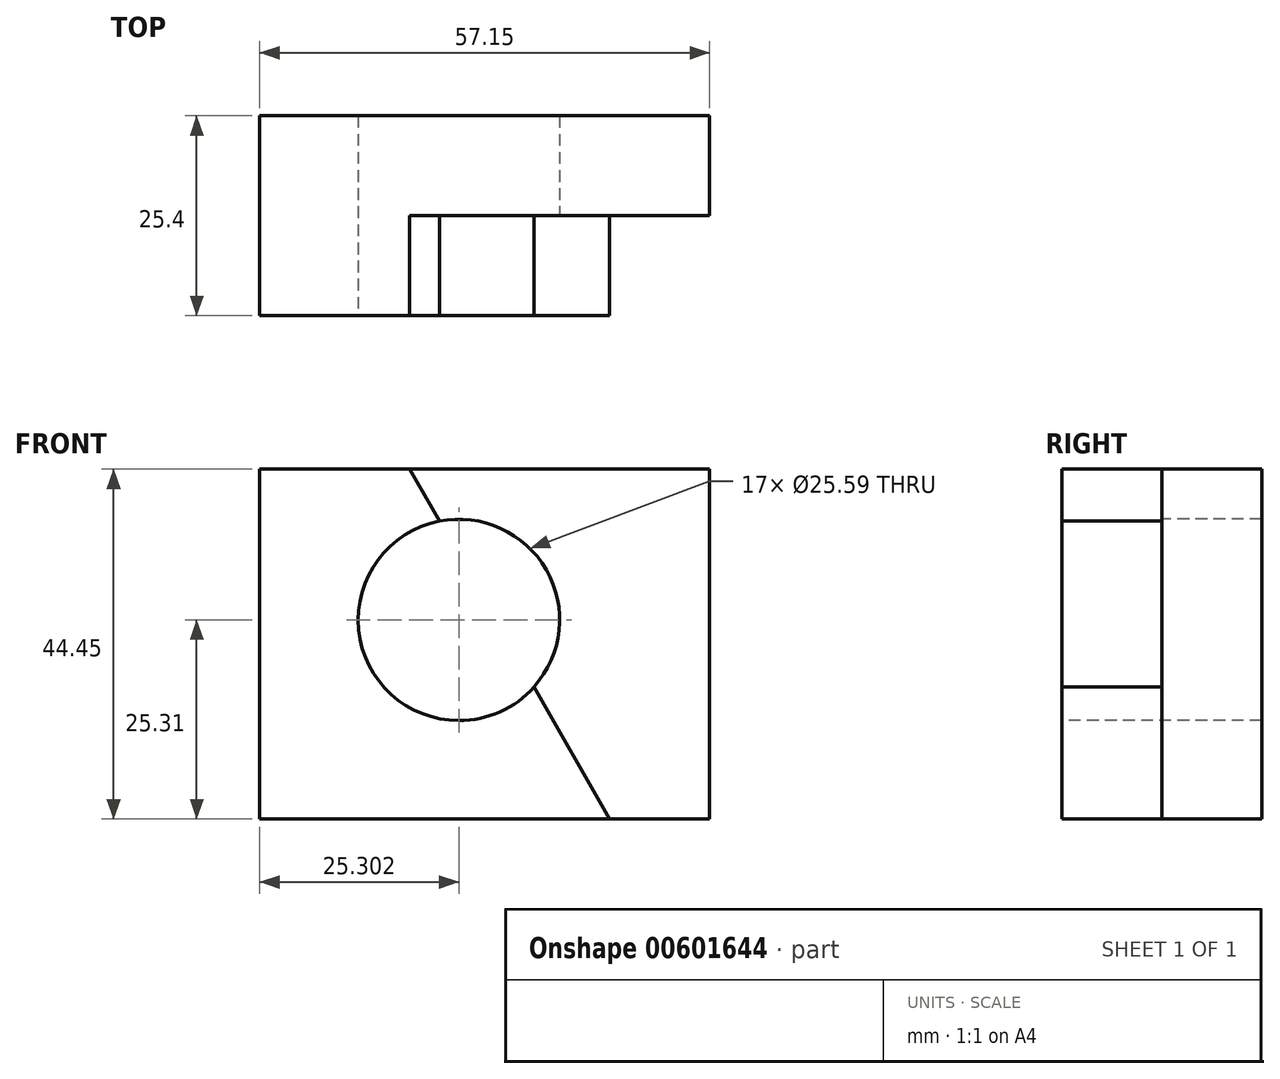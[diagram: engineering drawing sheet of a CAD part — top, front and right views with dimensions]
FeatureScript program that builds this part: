
annotation { "Feature Type Name" : "Feature", "Feature Type Description" : "" }
export const myFeature = defineFeature(function(context is Context, id is Id, definition is map)
    precondition{}
    {
        {
            var Q0;
            Q0=qCreatedBy(makeId("Front.planeOp"),FACE);
            var sketch = newSketch(context, id + "F0", { "sketchPlane" : qUnion([Q0])});
            skLineSegment(sketch, "E0", {"start": v(-65.96, 58.63) * mm, "end": v(-65.96, 14.18) * mm});
            skLineSegment(sketch, "E1", {"start": v(-65.96, 14.18) * mm, "end": v(-8.81, 14.18) * mm});
            skLineSegment(sketch, "E2", {"start": v(-8.81, 14.18) * mm, "end": v(-8.81, 58.63) * mm});
            skLineSegment(sketch, "E3", {"start": v(-65.96, 58.63) * mm, "end": v(-8.81, 58.63) * mm});
            skSolve(sketch);
        }
        {
            var Q0;
            Q0 = qSketchRegion(id + "F0", true);
            extrude(context, id + "F1", {"entities" : qUnion([Q0]), "depth" : 25.4 * mm, "offsetDistance" : 25.4 * mm});
        }
        {
            var Q0;
            Q0=makeQuery(id+"F1.opExtrude","CAP_FACE",FACE,{"disambiguationData":[OSD([sQuery(id+"F0.wireOp",EDGE,"E0"),sQuery(id+"F0.wireOp",EDGE,"E1"),sQuery(id+"F0.wireOp",EDGE,"E2"),sQuery(id+"F0.wireOp",EDGE,"E3")])],"isStart":false});
            var sketch = newSketch(context, id + "F2", { "sketchPlane" : qUnion([Q0])});
            skCircle(sketch, "E4", {"center": v(-40.66, 39.49) * mm, "radius": 12.8 * mm});
            skSolve(sketch);
        }
        {
            var Q0;
            Q0 = qSketchRegion(id + "F2", true);
            extrude(context, id + "F3", {"entities" : qUnion([Q0]), "operationType" : NewBodyOperationType.REMOVE, "oppositeDirection" : true, "depth" : 25.4 * mm, "offsetDistance" : 25.4 * mm});
        }
        {
            var Q0;
            Q0=makeQuery(id+"F1.opExtrude","SWEPT_FACE",FACE,{"disambiguationData":[OSD([sQuery(id+"F0.wireOp",EDGE,"E3")])]});
            var sketch = newSketch(context, id + "F4", { "sketchPlane" : qUnion([Q0])});
            skLineSegment(sketch, "E5", {"start": v(-21.51, -25.4) * mm, "end": v(-21.51, -12.7) * mm});
            skPoint(sketch, "E5.endSnap0", {"position": v(-65.96, -12.7) * mm});
            skLineSegment(sketch, "E6", {"start": v(-21.51, -12.7) * mm, "end": v(-8.81, -12.7) * mm});
            skLineSegment(sketch, "E7", {"start": v(-8.81, -12.7) * mm, "end": v(-8.81, -25.4) * mm});
            skLineSegment(sketch, "E8", {"start": v(-8.81, -25.4) * mm, "end": v(-21.51, -25.4) * mm});
            skSolve(sketch);
        }
        {
            var Q0;
            Q0 = qSketchRegion(id + "F4", true);
            extrude(context, id + "F5", {"entities" : qUnion([Q0]), "operationType" : NewBodyOperationType.REMOVE, "oppositeDirection" : true, "depth" : 44.45 * mm, "offsetDistance" : 25.4 * mm});
        }
        {
            var Q0;
            Q0=makeQuery(id+"F1.opExtrude","CAP_FACE",FACE,{"disambiguationData":[OSD([sQuery(id+"F0.wireOp",EDGE,"E0"),sQuery(id+"F0.wireOp",EDGE,"E1"),sQuery(id+"F0.wireOp",EDGE,"E2"),sQuery(id+"F0.wireOp",EDGE,"E3")])],"isStart":false});
            var sketch = newSketch(context, id + "F6", { "sketchPlane" : qUnion([Q0])});
            skLineSegment(sketch, "E9", {"start": v(-46.91, 58.63) * mm, "end": v(-21.51, 14.18) * mm});
            skLineSegment(sketch, "E10", {"start": v(-21.51, 14.18) * mm, "end": v(-21.51, 58.63) * mm});
            skLineSegment(sketch, "E11", {"start": v(-21.51, 58.63) * mm, "end": v(-46.91, 58.63) * mm});
            skSolve(sketch);
        }
        {
            var Q0;
            Q0 = qSketchRegion(id + "F6", true);
            extrude(context, id + "F7", {"entities" : qUnion([Q0]), "operationType" : NewBodyOperationType.REMOVE, "oppositeDirection" : true, "depth" : 12.7 * mm, "offsetDistance" : 25.4 * mm});
        }
    });
